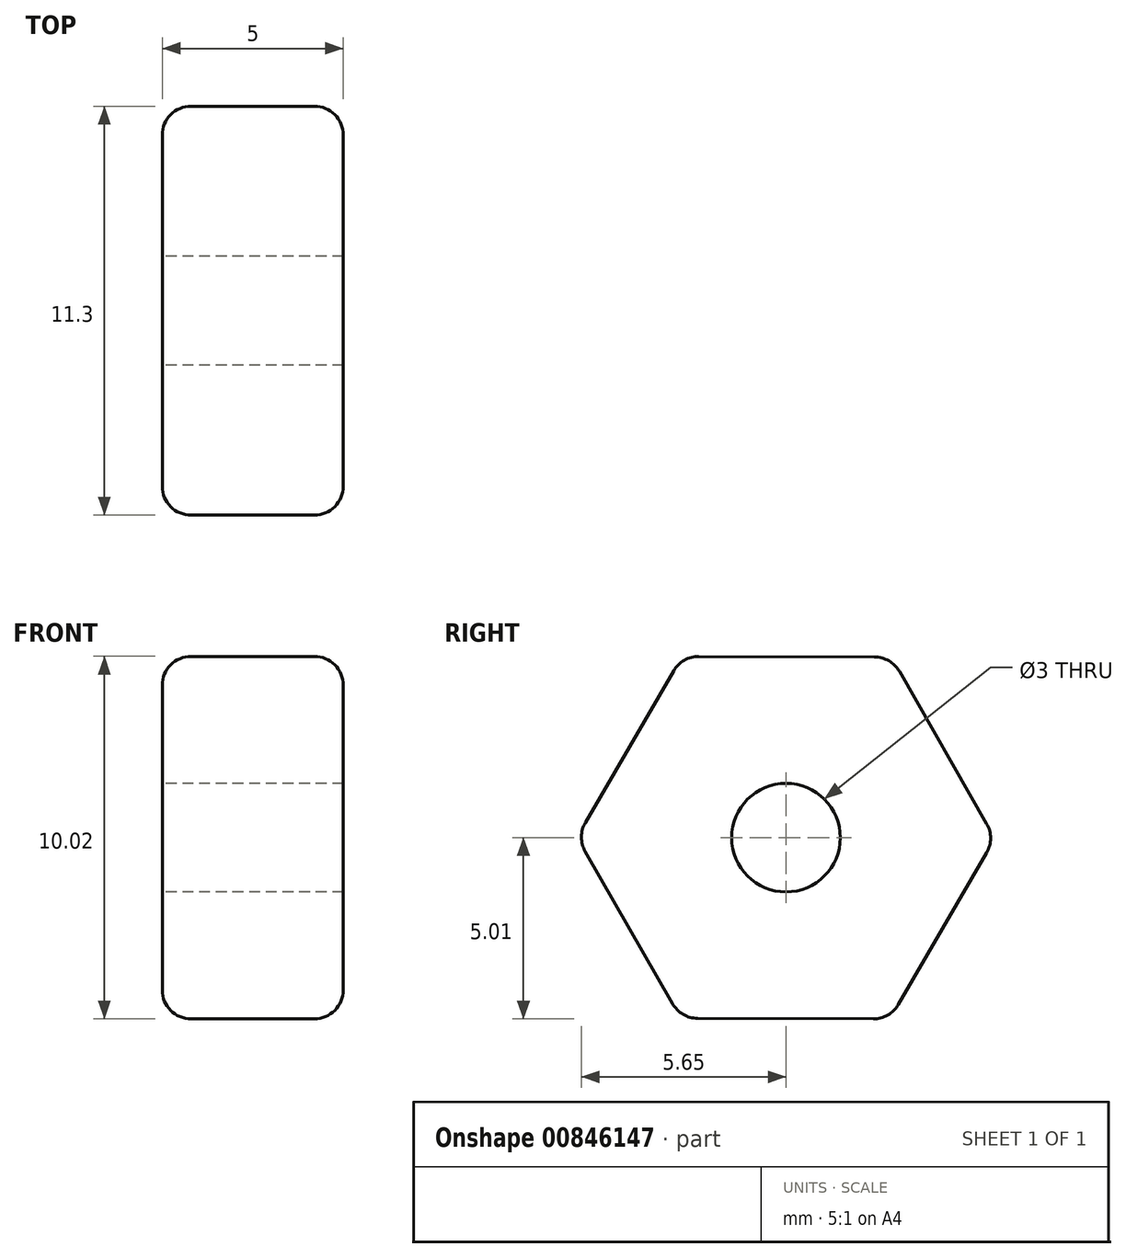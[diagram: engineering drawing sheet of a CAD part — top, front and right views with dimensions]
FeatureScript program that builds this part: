
annotation { "Feature Type Name" : "Feature", "Feature Type Description" : "" }
export const myFeature = defineFeature(function(context is Context, id is Id, definition is map)
    precondition{}
    {
        {
            var Q0;
            Q0=qCreatedBy(makeId("Right.planeOp"),FACE);
            var sketch = newSketch(context, id + "F0", { "sketchPlane" : qUnion([Q0])});
            skCircle(sketch, "E0.cCircle", {"center": v(0, 0) * mm, "radius": 5 * mm, "construction": true});
            skLineSegment(sketch, "E0.0", {"start": v(5.77, -0.02) * mm, "end": v(2.87, -5) * mm});
            skLineSegment(sketch, "E0.1", {"start": v(2.87, -5) * mm, "end": v(-2.9, -5) * mm});
            skLineSegment(sketch, "E0.2", {"start": v(-2.9, -5) * mm, "end": v(-5.77, 0.02) * mm});
            skLineSegment(sketch, "E0.3", {"start": v(-5.77, 0.02) * mm, "end": v(-2.87, 5) * mm});
            skLineSegment(sketch, "E0.4", {"start": v(-2.87, 5) * mm, "end": v(2.9, 5) * mm});
            skLineSegment(sketch, "E0.5", {"start": v(2.9, 5) * mm, "end": v(5.77, -0.02) * mm});
            skPoint(sketch, "E0.0.midPoint", {"position": v(4.32, -2.51) * mm});
            skCircle(sketch, "E1", {"center": v(0, 0) * mm, "radius": 1.5 * mm});
            skSolve(sketch);
        }
        {
            var Q0;
            Q0=makeQuery(id+"F0.imprint","IMPRINT",FACE,{"disambiguationData":[TD([[makeQuery(id+"F0.imprint","IMPRINT",EDGE,{"derivedFrom":sQuery(id+"F0.wireOp",EDGE,"E0.0")}),-1.0]])]});
            extrude(context, id + "F1", {"entities" : qUnion([Q0]), "depth" : 5 * mm, "offsetDistance" : 25 * mm});
        }
        {
            var Q0;
            Q0=makeQuery(id+"F1.opExtrude","SWEPT_EDGE",EDGE,{"disambiguationData":[OSD([sQuery(id+"F0.wireOp",EDGE,"E0.3"),sQuery(id+"F0.wireOp",EDGE,"E0.4")])]});
            var Q1;
            Q1=makeQuery(id+"F1.opExtrude","SWEPT_EDGE",EDGE,{"disambiguationData":[OSD([sQuery(id+"F0.wireOp",EDGE,"E0.4"),sQuery(id+"F0.wireOp",EDGE,"E0.5")])]});
            var Q2;
            Q2=makeQuery(id+"F1.opExtrude","SWEPT_EDGE",EDGE,{"disambiguationData":[OSD([sQuery(id+"F0.wireOp",EDGE,"E0.2"),sQuery(id+"F0.wireOp",EDGE,"E0.3")])]});
            var Q3;
            Q3=makeQuery(id+"F1.opExtrude","SWEPT_EDGE",EDGE,{"disambiguationData":[OSD([sQuery(id+"F0.wireOp",EDGE,"E0.1"),sQuery(id+"F0.wireOp",EDGE,"E0.2")])]});
            var Q4;
            Q4=makeQuery(id+"F1.opExtrude","SWEPT_EDGE",EDGE,{"disambiguationData":[OSD([sQuery(id+"F0.wireOp",EDGE,"E0.0"),sQuery(id+"F0.wireOp",EDGE,"E0.1")])]});
            var Q5;
            Q5=makeQuery(id+"F1.opExtrude","SWEPT_EDGE",EDGE,{"disambiguationData":[OSD([sQuery(id+"F0.wireOp",EDGE,"E0.0"),sQuery(id+"F0.wireOp",EDGE,"E0.5")])]});
            var Q6;
            Q6=makeQuery(id+"F1.opExtrude","CAP_EDGE",EDGE,{"disambiguationData":[OSD([sQuery(id+"F0.wireOp",EDGE,"E0.5")])],"isStart":false});
            var Q7;
            Q7=makeQuery(id+"F1.opExtrude","CAP_EDGE",EDGE,{"disambiguationData":[OSD([sQuery(id+"F0.wireOp",EDGE,"E0.5")])],"isStart":true});
            var Q8;
            Q8=makeQuery(id+"F1.opExtrude","CAP_EDGE",EDGE,{"disambiguationData":[OSD([sQuery(id+"F0.wireOp",EDGE,"E0.0")])],"isStart":false});
            var Q9;
            Q9=makeQuery(id+"F1.opExtrude","CAP_EDGE",EDGE,{"disambiguationData":[OSD([sQuery(id+"F0.wireOp",EDGE,"E0.0")])],"isStart":true});
            var Q10;
            Q10=makeQuery(id+"F1.opExtrude","CAP_EDGE",EDGE,{"disambiguationData":[OSD([sQuery(id+"F0.wireOp",EDGE,"E0.1")])],"isStart":false});
            var Q11;
            Q11=makeQuery(id+"F1.opExtrude","CAP_EDGE",EDGE,{"disambiguationData":[OSD([sQuery(id+"F0.wireOp",EDGE,"E0.1")])],"isStart":true});
            var Q12;
            Q12=makeQuery(id+"F1.opExtrude","CAP_EDGE",EDGE,{"disambiguationData":[OSD([sQuery(id+"F0.wireOp",EDGE,"E0.2")])],"isStart":false});
            var Q13;
            Q13=makeQuery(id+"F1.opExtrude","CAP_EDGE",EDGE,{"disambiguationData":[OSD([sQuery(id+"F0.wireOp",EDGE,"E0.2")])],"isStart":true});
            var Q14;
            Q14=makeQuery(id+"F1.opExtrude","CAP_EDGE",EDGE,{"disambiguationData":[OSD([sQuery(id+"F0.wireOp",EDGE,"E0.3")])],"isStart":false});
            var Q15;
            Q15=makeQuery(id+"F1.opExtrude","CAP_EDGE",EDGE,{"disambiguationData":[OSD([sQuery(id+"F0.wireOp",EDGE,"E0.3")])],"isStart":true});
            var Q16;
            Q16=makeQuery(id+"F1.opExtrude","CAP_EDGE",EDGE,{"disambiguationData":[OSD([sQuery(id+"F0.wireOp",EDGE,"E0.4")])],"isStart":true});
            var Q17;
            Q17=makeQuery(id+"F1.opExtrude","CAP_EDGE",EDGE,{"disambiguationData":[OSD([sQuery(id+"F0.wireOp",EDGE,"E0.4")])],"isStart":false});
            fillet(context, id + "F2", {"entities" : qUnion([Q0, Q1, Q2, Q3, Q4, Q5, Q6, Q7, Q8, Q9, Q10, Q11, Q12, Q13, Q14, Q15, Q16, Q17]), "radius" : 0.8 * mm, "tangentPropagation" : true, "allowEdgeOverflow" : false});
        }
    });
